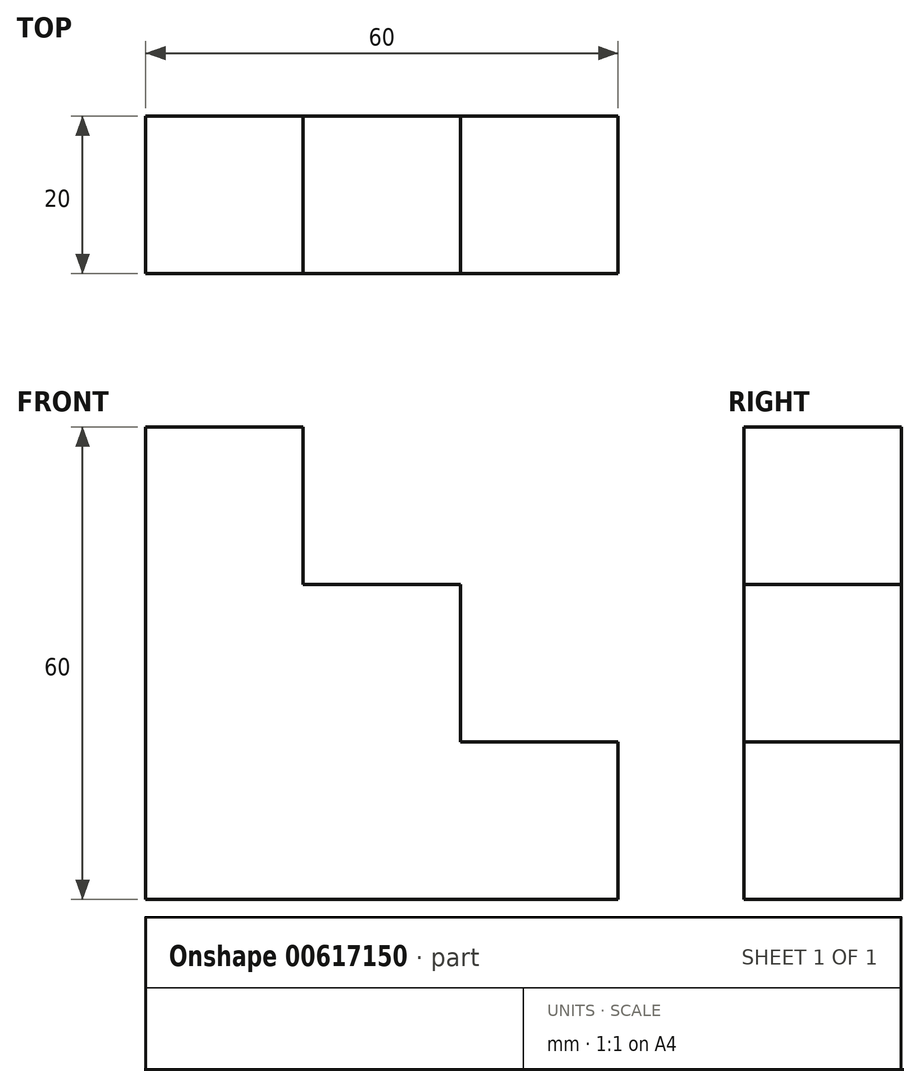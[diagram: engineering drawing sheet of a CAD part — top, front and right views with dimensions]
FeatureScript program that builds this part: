
annotation { "Feature Type Name" : "Feature", "Feature Type Description" : "" }
export const myFeature = defineFeature(function(context is Context, id is Id, definition is map)
    precondition{}
    {
        {
            var Q0;
            Q0=qCreatedBy(makeId("Front.planeOp"),FACE);
            var sketch = newSketch(context, id + "F0", { "sketchPlane" : qUnion([Q0])});
            skLineSegment(sketch, "E0", {"start": v(-42.9, 30.5) * mm, "end": v(-22.9, 30.5) * mm});
            skLineSegment(sketch, "E1", {"start": v(-22.9, 30.5) * mm, "end": v(-22.9, 10.5) * mm});
            skLineSegment(sketch, "E2", {"start": v(-22.9, 10.5) * mm, "end": v(-2.9, 10.5) * mm});
            skLineSegment(sketch, "E3", {"start": v(-2.9, 10.5) * mm, "end": v(-2.9, -9.5) * mm});
            skLineSegment(sketch, "E4", {"start": v(-2.9, -9.5) * mm, "end": v(17.1, -9.5) * mm});
            skLineSegment(sketch, "E5", {"start": v(17.1, -9.5) * mm, "end": v(17.1, -29.5) * mm});
            skLineSegment(sketch, "E6", {"start": v(17.1, -29.5) * mm, "end": v(-42.9, -29.5) * mm});
            skLineSegment(sketch, "E7", {"start": v(-42.9, -29.5) * mm, "end": v(-42.9, 30.5) * mm});
            skSolve(sketch);
        }
        {
            var Q0;
            Q0 = qSketchRegion(id + "F0", true);
            extrude(context, id + "F1", {"entities" : qUnion([Q0]), "depth" : 20 * mm, "offsetDistance" : 25 * mm});
        }
    });
